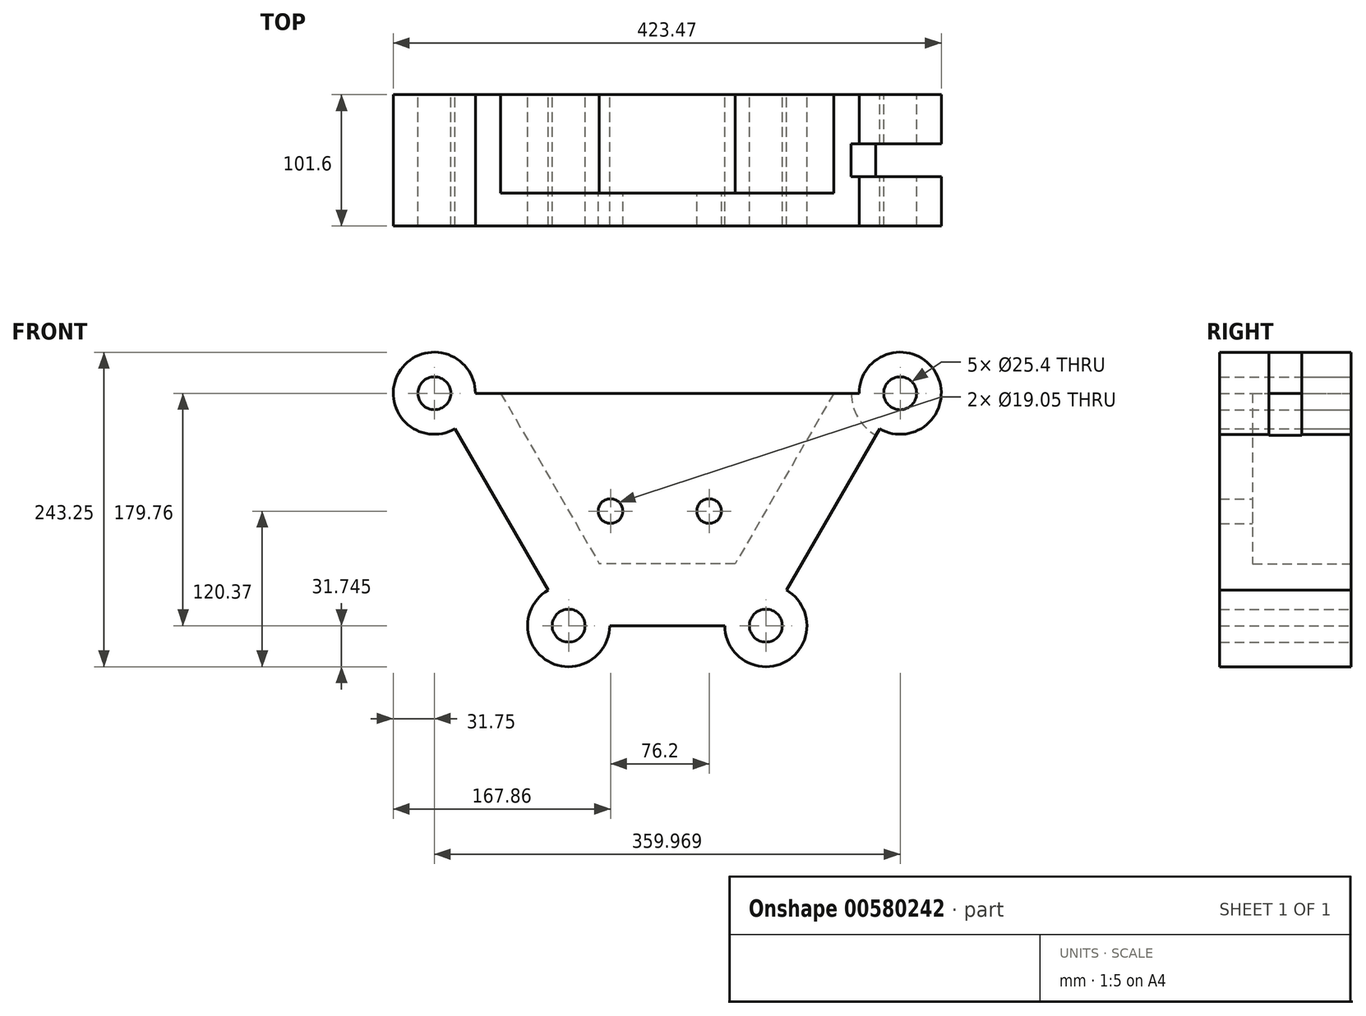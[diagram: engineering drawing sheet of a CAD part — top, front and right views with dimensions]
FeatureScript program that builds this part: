
annotation { "Feature Type Name" : "Feature", "Feature Type Description" : "" }
export const myFeature = defineFeature(function(context is Context, id is Id, definition is map)
    precondition{}
    {
        {
            var Q0;
            Q0=qCreatedBy(makeId("Front.planeOp"),FACE);
            var sketch = newSketch(context, id + "F0", { "sketchPlane" : qUnion([Q0])});
            skArc(sketch, "E0", {"start": v(-142.46, 91.13) * mm, "mid": v(-201.7, 107) * mm, "end": v(-158.33, 63.64) * mm});
            skCircle(sketch, "E1", {"center": v(-174.2, 91.13) * mm, "radius": 12.7 * mm});
            skArc(sketch, "E2", {"start": v(169.88, 63.64) * mm, "mid": v(213.26, 107) * mm, "end": v(154, 91.13) * mm});
            skCircle(sketch, "E3", {"center": v(185.76, 91.13) * mm, "radius": 12.7 * mm});
            skArc(sketch, "E4", {"start": v(50.22, -88.62) * mm, "mid": v(97.85, -116.12) * mm, "end": v(97.85, -61.13) * mm});
            skCircle(sketch, "E5", {"center": v(81.97, -88.62) * mm, "radius": 12.7 * mm});
            skArc(sketch, "E6", {"start": v(-86.3, -61.13) * mm, "mid": v(-86.3, -116.12) * mm, "end": v(-38.68, -88.62) * mm});
            skCircle(sketch, "E7", {"center": v(-70.43, -88.62) * mm, "radius": 12.7 * mm});
            skLineSegment(sketch, "E8.trimOffspring", {"start": v(-86.3, -61.13) * mm, "end": v(-158.33, 63.64) * mm});
            skLineSegment(sketch, "E9.trimOffspring", {"start": v(-38.68, -88.62) * mm, "end": v(50.22, -88.62) * mm});
            skLineSegment(sketch, "E10.trimOffspring", {"start": v(97.85, -61.13) * mm, "end": v(169.88, 63.64) * mm});
            skLineSegment(sketch, "E11.trimOffspring", {"start": v(-142.46, 91.13) * mm, "end": v(154, 91.13) * mm});
            skSolve(sketch);
        }
        {
            var Q0;
            Q0=qSketchRegion(id+"F0",true);
            extrude(context, id + "F1", {"entities" : qUnion([Q0]), "endBound" : BoundingType.SYMMETRIC, "depth" : -101.6 * mm, "offsetDistance" : 25.4 * mm});
        }
        {
            var Q0;
            Q0=makeQuery(id+"F1.opExtrude","CAP_FACE",FACE,{"disambiguationData":[OSD([sQuery(id+"F0.wireOp",EDGE,"E0"),sQuery(id+"F0.wireOp",EDGE,"E1"),sQuery(id+"F0.wireOp",EDGE,"E2"),sQuery(id+"F0.wireOp",EDGE,"E3"),sQuery(id+"F0.wireOp",EDGE,"E4"),sQuery(id+"F0.wireOp",EDGE,"E5"),sQuery(id+"F0.wireOp",EDGE,"E6"),sQuery(id+"F0.wireOp",EDGE,"E7"),sQuery(id+"F0.wireOp",EDGE,"E8.trimOffspring"),sQuery(id+"F0.wireOp",EDGE,"E9.trimOffspring"),sQuery(id+"F0.wireOp",EDGE,"E10.trimOffspring"),sQuery(id+"F0.wireOp",EDGE,"E11.trimOffspring")])],"isStart":true});
            var sketch = newSketch(context, id + "F2", { "sketchPlane" : qUnion([Q0])});
            skLineSegment(sketch, "E12", {"start": v(-134.43, 91.13) * mm, "end": v(-58.23, -40.85) * mm});
            skLineSegment(sketch, "E13", {"start": v(122.88, 91.13) * mm, "end": v(46.68, -40.85) * mm});
            skLineSegment(sketch, "E14", {"start": v(-58.23, -40.85) * mm, "end": v(46.68, -40.85) * mm});
            skSolve(sketch);
        }
        {
            var Q0;
            Q0=qSketchRegion(id+"F2",true);
            var Q1;
            {var subQ0=sQuery(id+"F2.wireOp",EDGE,"E12");Q1=makeQuery(id+"F2.imprint","IMPRINT",FACE,{"disambiguationData":[TD([[makeQuery(id+"F2.imprint","IMPRINT",EDGE,{"derivedFrom":subQ0}),1.0]])]});}
            extrude(context, id + "F3", {"entities" : qUnion([Q0, Q1]), "operationType" : NewBodyOperationType.REMOVE, "oppositeDirection" : true, "depth" : 76.2 * mm, "offsetDistance" : 25.4 * mm});
        }
        {
            var Q0;
            Q0=qCreatedBy(makeId("Front.planeOp"),FACE);
            var sketch = newSketch(context, id + "F4", { "sketchPlane" : qUnion([Q0])});
            skCircle(sketch, "E15", {"center": v(186.03, 91.58) * mm, "radius": 38.1 * mm});
            skSolve(sketch);
        }
        {
            var Q0;
            Q0=qSketchRegion(id+"F4",true);
            extrude(context, id + "F5", {"entities" : qUnion([Q0]), "operationType" : NewBodyOperationType.REMOVE, "endBound" : BoundingType.SYMMETRIC, "oppositeDirection" : true, "depth" : 25.4 * mm, "offsetDistance" : 25.4 * mm});
        }
        {
            var Q0;
            Q0=makeQuery(id+"F3.boolean.opBoolean","COPY",FACE,{"derivedFrom":makeQuery(id+"F3.opExtrude","CAP_FACE",FACE,{"disambiguationData":[OSD([sQuery(id+"F0.wireOp",EDGE,"E11.trimOffspring"),sQuery(id+"F2.wireOp",EDGE,"E12"),sQuery(id+"F2.wireOp",EDGE,"E13"),sQuery(id+"F2.wireOp",EDGE,"E14")])],"isStart":false})});
            var sketch = newSketch(context, id + "F6", { "sketchPlane" : qUnion([Q0])});
            skLineSegment(sketch, "E16", {"start": v(0, -24.33) * mm, "end": v(0, 10.34) * mm, "construction": true});
            skLineSegment(sketch, "E17", {"start": v(-38.1, 0) * mm, "end": v(38.1, 0) * mm});
            skCircle(sketch, "E18", {"center": v(38.1, 0) * mm, "radius": 9.53 * mm});
            skCircle(sketch, "E19", {"center": v(-38.1, 0) * mm, "radius": 9.53 * mm});
            skSolve(sketch);
        }
        {
            var Q0;
            Q0=qSketchRegion(id+"F6",true);
            extrude(context, id + "F7", {"entities" : qUnion([Q0]), "operationType" : NewBodyOperationType.REMOVE, "endBound" : BoundingType.SYMMETRIC, "oppositeDirection" : true, "depth" : 84.84 * mm, "offsetDistance" : 25.4 * mm});
        }
        {
            var Q0;
            Q0=sQuery(id+"F0.wireOp",EDGE,"E0");
            extrude(context, id + "F8", {"bodyType" : ToolBodyType.SURFACE, "surfaceEntities" : qUnion([Q0]), "depth" : 25.4 * mm, "offsetDistance" : 25.4 * mm});
        }
    });
